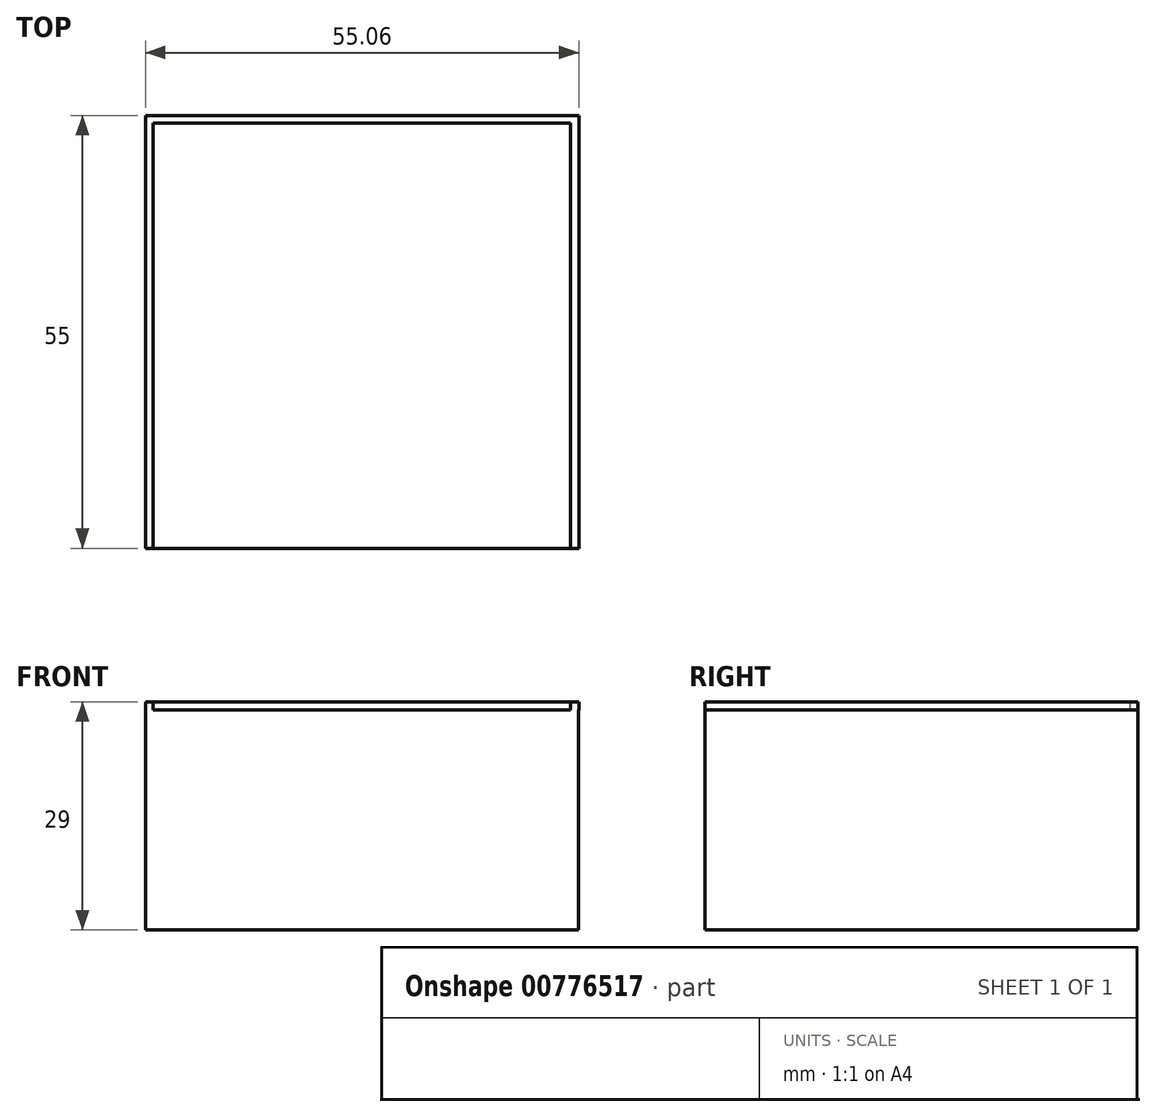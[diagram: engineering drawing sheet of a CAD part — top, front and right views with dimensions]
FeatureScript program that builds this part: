
annotation { "Feature Type Name" : "Feature", "Feature Type Description" : "" }
export const myFeature = defineFeature(function(context is Context, id is Id, definition is map)
    precondition{}
    {
        {
            var Q0;
            Q0=qCreatedBy(makeId("Top.planeOp"),FACE);
            var sketch = newSketch(context, id + "F0", { "sketchPlane" : qUnion([Q0])});
            skLineSegment(sketch, "E0.bottom", {"start": v(0, 0) * mm, "end": v(55, 0) * mm});
            skLineSegment(sketch, "E0.top", {"start": v(0, -55) * mm, "end": v(55, -55) * mm});
            skLineSegment(sketch, "E0.left", {"start": v(0, 0) * mm, "end": v(0, -55) * mm});
            skLineSegment(sketch, "E0.right", {"start": v(55, 0) * mm, "end": v(55, -55) * mm});
            skSolve(sketch);
        }
        {
            var Q0;
            Q0=makeQuery(id+"F0.imprint","IMPRINT",FACE,{"disambiguationData":[TD([[makeQuery(id+"F0.imprint","IMPRINT",EDGE,{"derivedFrom":sQuery(id+"F0.wireOp",EDGE,"E0.bottom")}),-1.0]])]});
            var sketch = newSketch(context, id + "F1", { "sketchPlane" : qUnion([Q0])});
            skLineSegment(sketch, "E1.0", {"start": v(54, -1) * mm, "end": v(54, -55) * mm});
            skLineSegment(sketch, "E1.1", {"start": v(1, -1) * mm, "end": v(54, -1) * mm});
            skLineSegment(sketch, "E1.2", {"start": v(1, -1) * mm, "end": v(1, -55) * mm});
            skLineSegment(sketch, "E2", {"start": v(1, -55) * mm, "end": v(0, -55) * mm});
            skLineSegment(sketch, "E3", {"start": v(0, -55) * mm, "end": v(0, 0) * mm});
            skLineSegment(sketch, "E4", {"start": v(0, 0) * mm, "end": v(55.06, 0) * mm});
            skLineSegment(sketch, "E5", {"start": v(55.06, 0) * mm, "end": v(55.06, -55) * mm});
            skLineSegment(sketch, "E6", {"start": v(54, -55) * mm, "end": v(55.06, -55) * mm});
            skSolve(sketch);
        }
        {
            var Q0;
            Q0=qSketchRegion(id+"F1",true);
            extrude(context, id + "F2", {"entities" : qUnion([Q0]), "depth" : 1 * mm, "offsetDistance" : 25 * mm});
        }
        {
            var Q0;
            Q0=qSketchRegion(id+"F0",true);
            extrude(context, id + "F3", {"entities" : qUnion([Q0]), "operationType" : NewBodyOperationType.ADD, "oppositeDirection" : true, "depth" : 28 * mm, "offsetDistance" : 25 * mm});
        }
    });
